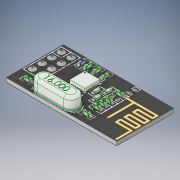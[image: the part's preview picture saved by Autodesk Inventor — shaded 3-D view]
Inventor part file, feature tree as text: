
AUTODESK INVENTOR PART (.ipt)
format: ipt  version: 2019.4 (Build 234330000, 330)  size: 6,866,944 bytes
history: mixed  units: mm
features: other x99, loft x29, boolean_combine x2, imported_body x1
ambient origin geometry x8: Origin, YZ Plane, XZ Plane, XY Plane, X Axis, Y Axis, Z Axis, Center Point
bodies: Solid1 (imported_parasolid), Solid2 (imported_parasolid), Solid3 (imported_parasolid), Solid4 (imported_parasolid), Solid5 (imported_parasolid), Solid6 (imported_parasolid), Solid7 (imported_parasolid), Solid8 (imported_parasolid), Solid9 (imported_parasolid), Solid10 (imported_parasolid), Solid11 (imported_parasolid), Solid12 (imported_parasolid), Solid13 (imported_parasolid), Solid14 (imported_parasolid), Solid15 (imported_parasolid), Solid16 (imported_parasolid), Solid17 (imported_parasolid), Solid18 (imported_parasolid), Solid19 (imported_parasolid), Solid20 (imported_parasolid), Solid21 (imported_parasolid), Solid22 (imported_parasolid), Solid23 (imported_parasolid), Solid24 (imported_parasolid), Solid25 (imported_parasolid), Solid26 (imported_parasolid), Solid27 (imported_parasolid), Solid28 (imported_parasolid), Solid29 (imported_parasolid), Solid30 (imported_parasolid), Solid31 (imported_parasolid), Solid32 (imported_parasolid), Solid33 (imported_parasolid), Solid34 (imported_parasolid), Solid35 (imported_parasolid), Solid36 (imported_parasolid), Solid37 (imported_parasolid), Solid38 (imported_parasolid), Solid39 (imported_parasolid), Solid40 (imported_parasolid), Solid41 (imported_parasolid), Solid42 (imported_parasolid), Solid43 (imported_parasolid), Solid44 (imported_parasolid), Solid45 (imported_parasolid), Solid46 (imported_parasolid), Solid47 (imported_parasolid), Solid48 (imported_parasolid), Solid49 (imported_parasolid), Solid50 (imported_parasolid), Solid51 (imported_parasolid), Solid52 (imported_parasolid), Solid53 (imported_parasolid), Solid54 (imported_parasolid), Solid55 (imported_parasolid), Solid56 (imported_parasolid), Solid57 (imported_parasolid), Solid58 (imported_parasolid), Solid59 (imported_parasolid), Solid60 (imported_parasolid), Solid61 (imported_parasolid), Solid62 (imported_parasolid), Solid63 (imported_parasolid), Solid64 (imported_parasolid), Solid65 (imported_parasolid), Solid66 (imported_parasolid), Solid67 (imported_parasolid), Solid68 (imported_parasolid), Solid69 (imported_parasolid), Solid70 (imported_parasolid), Solid71 (imported_parasolid), Solid72 (imported_parasolid), Solid73 (imported_parasolid), Solid74 (imported_parasolid), Solid75 (imported_parasolid), Solid76 (imported_parasolid), Solid77 (imported_parasolid), Solid78 (imported_parasolid), Solid79 (imported_parasolid), Solid80 (imported_parasolid), Solid81 (imported_parasolid), Solid82 (imported_parasolid), Solid83 (imported_parasolid), Solid84 (imported_parasolid), Solid85 (imported_parasolid), Solid86 (imported_parasolid), Solid87 (imported_parasolid), Solid88 (imported_parasolid), Solid89 (imported_parasolid), Solid90 (imported_parasolid), Solid91 (imported_parasolid), Solid92 (imported_parasolid), Solid93 (imported_parasolid), Solid94 (imported_parasolid), Solid95 (imported_parasolid), Solid96 (imported_parasolid), Solid97 (imported_parasolid), Solid98 (imported_parasolid), Solid99 (imported_parasolid), Solid100 (imported_parasolid), Solid101 (imported_parasolid), Solid102 (imported_parasolid), Solid103 (imported_parasolid), Solid104 (imported_parasolid), Solid105 (imported_parasolid), Solid106 (imported_parasolid), Solid107 (imported_parasolid), Solid108 (imported_parasolid), Solid109 (imported_parasolid), Solid110 (imported_parasolid), Solid111 (imported_parasolid), Solid112 (imported_parasolid), Solid113 (imported_parasolid), Solid114 (imported_parasolid), Solid115 (imported_parasolid), Solid116 (imported_parasolid), Solid117 (imported_parasolid), Solid118 (imported_parasolid), Solid119 (imported_parasolid), Solid120 (imported_parasolid), Solid121 (imported_parasolid), Solid122 (imported_parasolid), Solid123 (imported_parasolid), Solid124 (imported_parasolid), Solid125 (imported_parasolid), Solid126 (imported_parasolid), Solid127 (imported_parasolid), Solid128 (imported_parasolid), Solid129 (imported_parasolid), Solid130 (imported_parasolid)
feature tree (131):
  other  "PCB Body"
  other  "Cut-Extrude1[2]"
  other  "Cut-Extrude1[3]"
  other  "Cut-Extrude1[4]"
  other  "Cut-Extrude1[5]"
  other  "Cut-Extrude1[6]"
  other  "Cut-Extrude1[7]"
  other  "Cut-Extrude1[8]"
  other  "Cut-Extrude1[9]"
  other  "Cut-Extrude1[10]"
  other  "Cut-Extrude1[11]"
  other  "Cut-Extrude1[12]"
  other  "Cut-Extrude1[13]"
  other  "Cut-Extrude2[1]"
  other  "Cut-Extrude2[2]"
  other  "Cut-Extrude2[3]"
  other  "Cut-Extrude2[4]"
  other  "_Capacitor 1608_-_Solid7_"
  other  "Body-Move_Copy21"
  other  "Body-Move_Copy22"
  other  "_Resistor 1608_-_Imported1_"
  other  "Body-Move_Copy26"
  other  "Body-Move_Copy28"
  other  "Body-Move_Copy29[1]"
  other  "Body-Move_Copy29[2]"
  other  "Body-Move_Copy30"
  other  "Body-Move_Copy31"
  other  "Body-Move_Copy34"
  other  "_rg1608p-103-b_-_rg1608p-103-b_"
  other  "Body-Move_Copy38"
  other  "Body-Move_Copy39"
  other  "_QFN-20 with Pad_-_Вытянуть4_"
  other  "Boss-Extrude22"
  other  "Boss-Extrude28"
  other  "Body-Move_Copy50"
  other  "Boss-Extrude31"
  other  "Cut-Extrude3"
  loft  "Loft2"
  loft  "Loft4"
  loft  "Loft7"
  loft  "Loft9"
  loft  "Loft10"
  loft  "Loft12"
  loft  "Loft13"
  loft  "Loft14"
  loft  "Loft15"
  loft  "Loft16"
  loft  "Loft17"
  loft  "Loft18"
  loft  "Loft19"
  loft  "Loft20"
  loft  "Loft21"
  loft  "Loft22"
  loft  "Loft23"
  loft  "Loft24"
  loft  "Loft25"
  loft  "Loft26"
  loft  "Loft27"
  loft  "Loft28"
  loft  "Loft29"
  loft  "Loft30"
  loft  "Loft31"
  loft  "Loft32"
  loft  "Loft33"
  loft  "Loft34"
  loft  "Loft35"
  other  "Body-Move_Copy51[1]"
  other  "Body-Move_Copy51[2]"
  other  "Body-Move_Copy51[3]"
  other  "Body-Move_Copy51[4]"
  other  "Body-Move_Copy53[1]"
  other  "Body-Move_Copy53[2]"
  other  "Body-Move_Copy53[3]"
  other  "Body-Move_Copy53[4]"
  other  "Body-Move_Copy53[5]"
  other  "Body-Move_Copy57[1]"
  other  "Body-Move_Copy57[2]"
  other  "Body-Move_Copy57[3]"
  other  "Body-Move_Copy57[4]"
  other  "Body-Move_Copy57[5]"
  other  "Body-Move_Copy57[6]"
  other  "Body-Move_Copy57[7]"
  other  "Body-Move_Copy57[8]"
  other  "Body-Move_Copy57[9]"
  other  "Body-Move_Copy57[10]"
  other  "Boss-Extrude38[1]"
  other  "Boss-Extrude38[2]"
  other  "Boss-Extrude38[3]"
  other  "Boss-Extrude38[4]"
  other  "Cut-Extrude4[1]"
  other  "Cut-Extrude4[2]"
  other  "_Header 2_54 Vertical 1x2_-_Chamfer2_"
  other  "Cut-Extrude5[1]"
  other  "Cut-Extrude5[2]"
  other  "Cut-Extrude5[3]"
  other  "Cut-Extrude5[4]"
  other  "Cut-Extrude5[5]"
  other  "Cut-Extrude5[6]"
  other  "Cut-Extrude5[7]"
  other  "Cut-Extrude5[8]"
  other  "Boss-Extrude43"
  other  "Boss-Extrude45[1]"
  other  "Boss-Extrude45[2]"
  other  "Boss-Extrude45[3]"
  other  "Boss-Extrude45[4]"
  other  "Boss-Extrude45[5]"
  other  "Boss-Extrude45[6]"
  other  "Boss-Extrude45[7]"
  other  "Boss-Extrude45[8]"
  other  "Boss-Extrude45[9]"
  other  "Boss-Extrude45[10]"
  other  "Boss-Extrude45[11]"
  other  "Boss-Extrude45[12]"
  other  "Boss-Extrude45[13]"
  other  "Boss-Extrude45[14]"
  other  "Boss-Extrude45[15]"
  other  "Boss-Extrude45[16]"
  other  "Boss-Extrude45[17]"
  other  "Boss-Extrude45[18]"
  other  "Boss-Extrude45[19]"
  other  "Boss-Extrude45[20]"
  other  "Boss-Extrude45[21]"
  other  "Boss-Extrude45[22]"
  other  "Boss-Extrude45[23]"
  other  "Boss-Extrude45[24]"
  boolean_combine  "Combine15"
  boolean_combine  "Combine16"
  other  "LPattern2[1]"
  other  "LPattern2[2]"
  other  "LPattern2[3]"
  imported_body  NMx_Import_Brep_tag  [imported B-rep: ~522 faces, bbox_mm=None]
